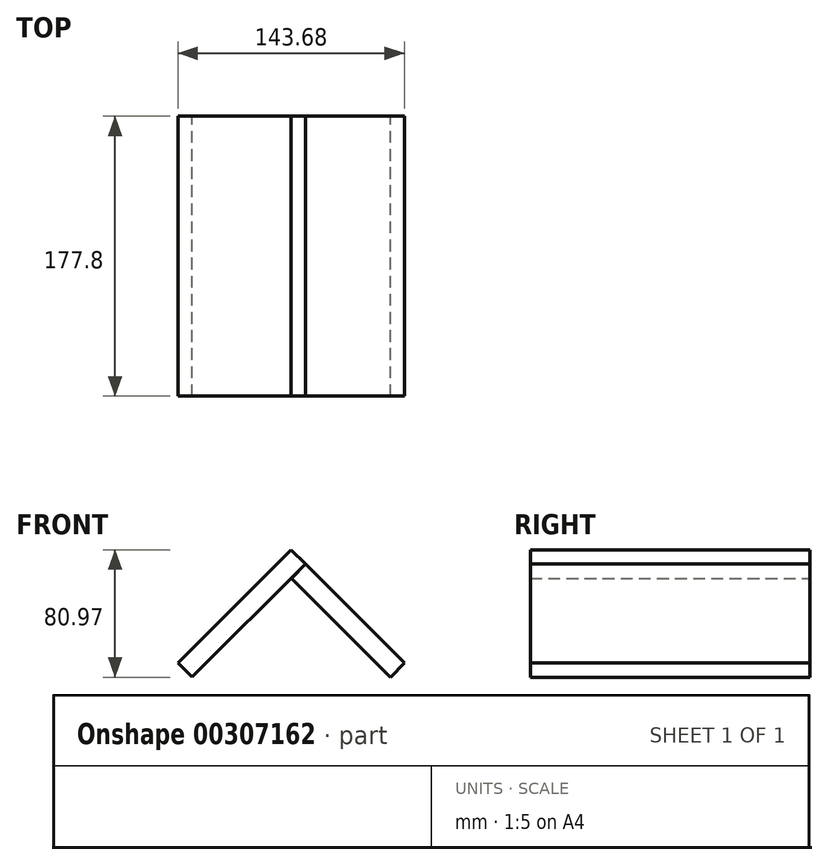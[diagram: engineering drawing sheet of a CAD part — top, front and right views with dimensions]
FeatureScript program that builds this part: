
annotation { "Feature Type Name" : "Feature", "Feature Type Description" : "" }
export const myFeature = defineFeature(function(context is Context, id is Id, definition is map)
    precondition{}
    {
        {
            var Q0;
            Q0=qCreatedBy(makeId("Front.planeOp"),FACE);
            var sketch = newSketch(context, id + "F0", { "sketchPlane" : qUnion([Q0])});
            skLineSegment(sketch, "E0", {"start": v(15.16, 7.52) * mm, "end": v(6.18, 16.5) * mm});
            skLineSegment(sketch, "E1", {"start": v(-56.68, -64.32) * mm, "end": v(-65.66, -55.34) * mm});
            skLineSegment(sketch, "E2", {"start": v(6.34, -1.61) * mm, "end": v(15.16, 7.52) * mm});
            skLineSegment(sketch, "E3", {"start": v(-65.66, -55.34) * mm, "end": v(6.18, 16.5) * mm});
            skLineSegment(sketch, "E4", {"start": v(15.16, 7.52) * mm, "end": v(78.02, -55.34) * mm});
            skLineSegment(sketch, "E5", {"start": v(69.2, -64.47) * mm, "end": v(78.02, -55.34) * mm});
            skLineSegment(sketch, "E6", {"start": v(6.34, -1.61) * mm, "end": v(69.2, -64.47) * mm});
            skLineSegment(sketch, "E7", {"start": v(-56.68, -64.32) * mm, "end": v(15.16, 7.52) * mm});
            skSolve(sketch);
        }
        {
            var Q0;
            Q0=makeQuery(id+"F0.imprint","IMPRINT",FACE,{"disambiguationData":[TD([[makeQuery(id+"F0.imprint","IMPRINT",EDGE,{"derivedFrom":sQuery(id+"F0.wireOp",EDGE,"E0")}),1.0]])]});
            var Q1;
            Q1=makeQuery(id+"F0.imprint","IMPRINT",FACE,{"disambiguationData":[TD([[makeQuery(id+"F0.imprint","IMPRINT",EDGE,{"derivedFrom":sQuery(id+"F0.wireOp",EDGE,"E2")}),-1.0]])]});
            extrude(context, id + "F1", {"entities" : qUnion([Q0, Q1]), "depth" : 177.8 * mm});
        }
    });
